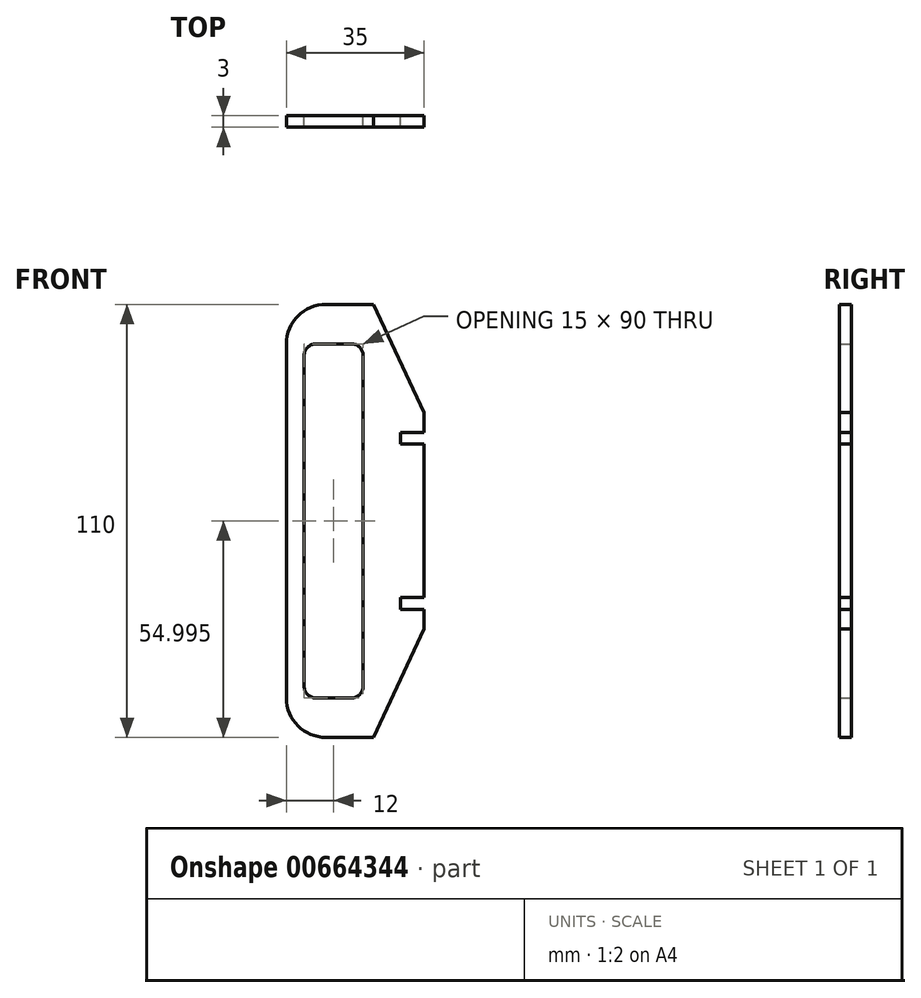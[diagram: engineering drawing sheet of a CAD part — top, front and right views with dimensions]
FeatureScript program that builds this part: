
annotation { "Feature Type Name" : "Feature", "Feature Type Description" : "" }
export const myFeature = defineFeature(function(context is Context, id is Id, definition is map)
    precondition{}
    {
        {
            var Q0;
            Q0=qCreatedBy(makeId("Front.planeOp"),FACE);
            var sketch = newSketch(context, id + "F0", { "sketchPlane" : qUnion([Q0])});
            skLineSegment(sketch, "E0", {"start": v(-47.27, 46.86) * mm, "end": v(-47.27, 1.86) * mm});
            skLineSegment(sketch, "E1", {"start": v(-12.27, 1.86) * mm, "end": v(-12.27, 21.36) * mm});
            skLineSegment(sketch, "E2", {"start": v(-25.1, 56.86) * mm, "end": v(-37.27, 56.86) * mm});
            skLineSegment(sketch, "E3", {"start": v(-25.1, 56.86) * mm, "end": v(-12.27, 29.36) * mm});
            skLineSegment(sketch, "E4", {"start": v(-12.27, 21.36) * mm, "end": v(-18.27, 21.36) * mm});
            skLineSegment(sketch, "E5", {"start": v(-18.27, 21.36) * mm, "end": v(-18.27, 24.36) * mm});
            skLineSegment(sketch, "E6", {"start": v(-18.27, 24.36) * mm, "end": v(-12.27, 24.36) * mm});
            skLineSegment(sketch, "E7.trimOffspring", {"start": v(-12.27, 24.36) * mm, "end": v(-12.27, 29.36) * mm});
            skLineSegment(sketch, "E8.bottom", {"start": v(-39.77, 46.86) * mm, "end": v(-30.77, 46.86) * mm});
            skLineSegment(sketch, "E8.left", {"start": v(-42.77, 43.86) * mm, "end": v(-42.77, 1.86) * mm});
            skLineSegment(sketch, "E8.right", {"start": v(-27.77, 43.86) * mm, "end": v(-27.77, 1.86) * mm});
            skPoint(sketch, "E9.visualSharp", {"position": v(-47.27, 56.86) * mm});
            skArc(sketch, "E9.filletArc", {"start": v(-37.27, 56.86) * mm, "mid": v(-44.34, 53.93) * mm, "end": v(-47.27, 46.86) * mm});
            skPoint(sketch, "E10.visualSharp", {"position": v(-42.77, 46.86) * mm});
            skArc(sketch, "E10.filletArc", {"start": v(-39.77, 46.86) * mm, "mid": v(-41.9, 45.98) * mm, "end": v(-42.77, 43.86) * mm});
            skPoint(sketch, "E11.visualSharp", {"position": v(-27.77, 46.86) * mm});
            skArc(sketch, "E11.filletArc", {"start": v(-27.77, 43.86) * mm, "mid": v(-28.65, 45.98) * mm, "end": v(-30.77, 46.86) * mm});
            skArc(sketch, "E12.MirrorCS", {"start": v(-27.77, -40.14) * mm, "mid": v(-28.65, -42.27) * mm, "end": v(-30.77, -43.14) * mm});
            skArc(sketch, "E13.MirrorCS", {"start": v(-39.77, -43.14) * mm, "mid": v(-41.9, -42.27) * mm, "end": v(-42.77, -40.14) * mm});
            skLineSegment(sketch, "E14.MirrorCS", {"start": v(-18.27, -17.64) * mm, "end": v(-18.27, -20.64) * mm});
            skLineSegment(sketch, "E15.MirrorCS", {"start": v(-18.27, -20.64) * mm, "end": v(-12.27, -20.64) * mm});
            skLineSegment(sketch, "E16.MirrorCS", {"start": v(-12.27, -20.64) * mm, "end": v(-12.27, -25.64) * mm});
            skLineSegment(sketch, "E17.MirrorCS", {"start": v(-12.27, -17.64) * mm, "end": v(-18.27, -17.64) * mm});
            skLineSegment(sketch, "E18.MirrorCS", {"start": v(-39.77, -43.14) * mm, "end": v(-30.77, -43.14) * mm});
            skLineSegment(sketch, "E19.MirrorCS", {"start": v(-42.77, -40.14) * mm, "end": v(-42.77, 1.86) * mm});
            skPoint(sketch, "E20.MirrorP", {"position": v(-27.77, -43.14) * mm});
            skPoint(sketch, "E21.MirrorP", {"position": v(-42.77, -43.14) * mm});
            skArc(sketch, "E22.MirrorCS", {"start": v(-37.27, -53.14) * mm, "mid": v(-44.34, -50.22) * mm, "end": v(-47.27, -43.14) * mm});
            skLineSegment(sketch, "E23.MirrorCS", {"start": v(-12.27, 1.86) * mm, "end": v(-12.27, -17.64) * mm});
            skLineSegment(sketch, "E24.MirrorCS", {"start": v(-47.27, -43.14) * mm, "end": v(-47.27, 1.86) * mm});
            skLineSegment(sketch, "E25.MirrorCS", {"start": v(-27.77, -40.14) * mm, "end": v(-27.77, 1.86) * mm});
            skLineSegment(sketch, "E26.MirrorCS", {"start": v(-25.1, -53.14) * mm, "end": v(-37.27, -53.14) * mm});
            skLineSegment(sketch, "E27.MirrorCS", {"start": v(-25.1, -53.14) * mm, "end": v(-12.27, -25.64) * mm});
            skPoint(sketch, "E28.MirrorP", {"position": v(-47.27, -53.14) * mm});
            skSolve(sketch);
        }
        {
            var Q0;
            Q0=makeQuery(id+"F0.imprint","IMPRINT",FACE,{"disambiguationData":[TD([[makeQuery(id+"F0.imprint","IMPRINT",EDGE,{"derivedFrom":sQuery(id+"F0.wireOp",EDGE,"E0")}),1.0]])]});
            extrude(context, id + "F1", {"entities" : qUnion([Q0]), "depth" : 3 * mm, "offsetDistance" : 25 * mm});
        }
    });
